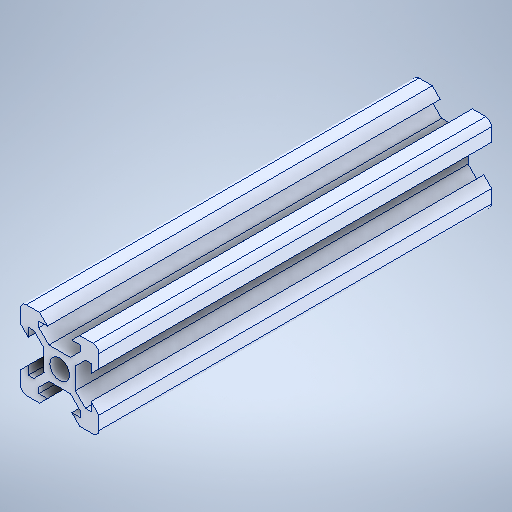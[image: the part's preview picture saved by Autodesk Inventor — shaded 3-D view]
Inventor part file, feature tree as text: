
AUTODESK INVENTOR PART (.ipt)
format: ipt  version: 2025.1 (Build 291241020, 241B)  size: 406,016 bytes
history: native  units: in
note: dims shown in document units (in); Inventor stores cm internally (conversion verified against a paired STEP export)
features: extrude x2, sketch x1, projected_geometry x1, other x1
ambient origin geometry x8: Origin, YZ Plane, XZ Plane, XY Plane, X Axis, Y Axis, Z Axis, Center Point
bodies: Solid1 (feature_tree)
feature tree (5):
  sketch  "Sketch1"  dims[d0=3.937in d1=0.0in d2=3.937in d3=0.0in]
  extrude  "Extrusion1"  Depth=3.937in TaperAngle=0.0deg
  extrude  "Extrusion2"  [1 undecoded]
  projected_geometry  "Projected Loop1"
  other  "Скругление1"
note: 1 required parameter value undecoded (feature->parameter linkage not recoverable at this tier; creation-order binding heuristic only, values carry confidence <= 0.55)
